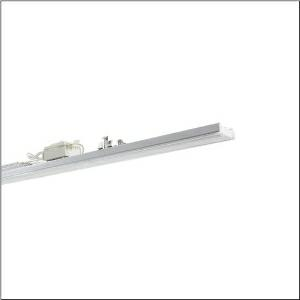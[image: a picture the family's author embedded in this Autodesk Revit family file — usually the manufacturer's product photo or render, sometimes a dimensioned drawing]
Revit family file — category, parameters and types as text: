
# Revit family: licross_r__21_recessed_mo_52tl18dv46xg_fa77
name_source: partatom
category: Lighting Fixtures
units: mm (PartAtom-declared; Revit-internal decimal feet)

## family parameters
Cut with Voids When Loaded = No
Host = Face
Light Source = No
Part Type = Normal
Room Calculation Point = No
Round Connector Dimension = Use Diameter
Shared = No

## types (1)
- --- (1 x LED, 6200 lm, 34.5 W, 4000K)
    Apparent Load = 35 VA
    CIE Flux Codes = 79 95 99 100 100
    Color Rendering = 80
    Color Temperature = 4000K
    Default Elevation = 1800 mm
    Description = Licross® 21 Recessed MO, luminaire insert, of sheet steel, galvanised, coil coated, white, length: 2.250mm, width: 66mm, height: 67mm, LED rated luminous flux: 6.200lm, light colour: 840, control gear: DALI 2, with plug, 5-pole, with phase selection, mains connection: 220..240V, AC, 50/60Hz, rated input power: 35W, internal wiring halogen-free, primary light control with lens, of plastic, primary optical cover: cover, of PMMA, light emission: direct distribution, primary light characteristic: symmetric, protection rating (complete): IP40, insulation class (complete): insulation class I (protective earthing), certification: CE, ENEC, VDE, UKCA, protection symbol: D if used in an environment without relevant dust loads with corresponding accessories, impact resistance: IK06, permissible ambient temperature for indoor applications: -25..+45°C, corresponds to IFS (International Featured Standards) requirements for safety and quality in the food industry, reducing of maximum allowable ambient temperature of 5°C with ceiling mounting, LABS conformity tested according to VDMA 24364:2018-05, packaging unit: 1 piece
    Height = 58 mm
    Lamp = 1 x LED
    Lamp Light Flux = 6200 lm
    Lamp Power = 34.5 W
    Lamp count = 1
    Length = 2250 mm
    Luminous efficacy = 180 lm/W
    Manufacturer = Siteco
    ModVariant = No
    Model = 52TL18DV46XG
    Mounting Place = Ceiling
    Mounting Type = Pendant
    Number of Poles = 1
    OnlyDefault = Yes
    Power Factor = 1
    Product Name = Licross® 21 Recessed MO
    Product group = luminaire insert | ceiling pendant
    ProductGroupID = 902
    Protection Class = Protection class I
    Protection Degree = IP 40
    RLX_Detail_Level = 1
    RLX_Emergency_Light_Flux = 0 lm
    RLX_Emergency_Type = 0
    RLX_Emergency_Type_DB = No
    RlxData = <blob elided: 28901 chars, md5=8665ee2d>
    Socket = socket
    Standby Power = 0 W
    System Light Flux = 6200 lm
    System Power = 35 W
    Type Comments = factory setting: luminous flux: 100 % | dim-lin: 254 | 154 mA
    Type Image = l_1296930.jpg
    URL = http://relux.com
    VarID = @adj_062551
    Voltage = 0 V
    Weight = 0.00 kg
    Width = 66 mm

## geometry (parser evidence)
native form markers: Blend x4, Sweep x9
no freeform markers — native parametric forms only
